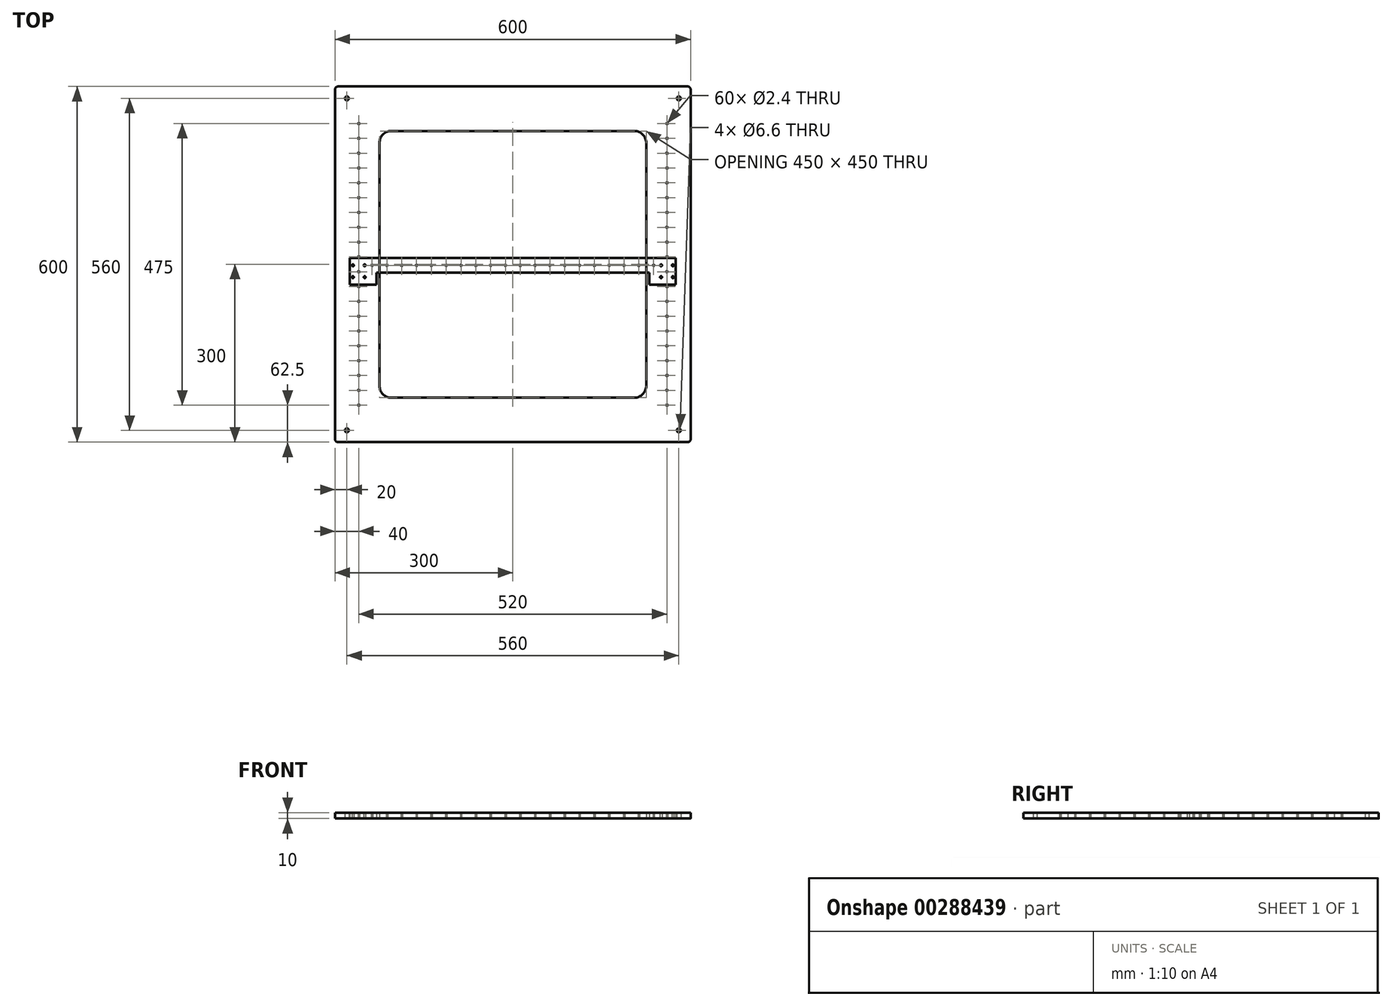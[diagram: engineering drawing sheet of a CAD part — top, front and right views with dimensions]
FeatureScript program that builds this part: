
annotation { "Feature Type Name" : "Feature", "Feature Type Description" : "" }
export const myFeature = defineFeature(function(context is Context, id is Id, definition is map)
    precondition{}
    {
        {
            var Q0;
            Q0=qCreatedBy(makeId("Top.planeOp"),FACE);
            var sketch = newSketch(context, id + "F0", { "sketchPlane" : qUnion([Q0])});
            skLineSegment(sketch, "E0.bottom", {"start": v(-295, 300) * mm, "end": v(295, 300) * mm});
            skLineSegment(sketch, "E0.top", {"start": v(-295, -300) * mm, "end": v(295, -300) * mm});
            skLineSegment(sketch, "E0.left", {"start": v(-300, 295) * mm, "end": v(-300, -295) * mm});
            skLineSegment(sketch, "E0.right", {"start": v(300, 295) * mm, "end": v(300, -295) * mm});
            skLineSegment(sketch, "E1", {"start": v(-260, 250) * mm, "end": v(-260, -250) * mm, "construction": true});
            skPoint(sketch, "E2", {"position": v(-260, -237.5) * mm});
            skPoint(sketch, "E3.0.1.0", {"position": v(-260, -212.5) * mm});
            skPoint(sketch, "E3.0.2.0", {"position": v(-260, -187.5) * mm});
            skPoint(sketch, "E3.0.3.0", {"position": v(-260, -162.5) * mm});
            skPoint(sketch, "E3.0.4.0", {"position": v(-260, -137.5) * mm});
            skPoint(sketch, "E3.0.5.0", {"position": v(-260, -112.5) * mm});
            skPoint(sketch, "E3.0.6.0", {"position": v(-260, -87.5) * mm});
            skPoint(sketch, "E3.0.7.0", {"position": v(-260, -62.5) * mm});
            skPoint(sketch, "E3.0.8.0", {"position": v(-260, -37.5) * mm});
            skPoint(sketch, "E3.0.9.0", {"position": v(-260, -12.5) * mm});
            skPoint(sketch, "E3.0.10.0", {"position": v(-260, 12.5) * mm});
            skPoint(sketch, "E3.0.11.0", {"position": v(-260, 37.5) * mm});
            skPoint(sketch, "E3.0.12.0", {"position": v(-260, 62.5) * mm});
            skPoint(sketch, "E3.0.13.0", {"position": v(-260, 87.5) * mm});
            skPoint(sketch, "E3.0.14.0", {"position": v(-260, 112.5) * mm});
            skPoint(sketch, "E3.0.15.0", {"position": v(-260, 137.5) * mm});
            skPoint(sketch, "E3.0.16.0", {"position": v(-260, 162.5) * mm});
            skPoint(sketch, "E3.0.17.0", {"position": v(-260, 187.5) * mm});
            skPoint(sketch, "E3.0.18.0", {"position": v(-260, 212.5) * mm});
            skPoint(sketch, "E3.0.19.0", {"position": v(-260, 237.5) * mm});
            skLineSegment(sketch, "E3.direction1", {"start": v(-260, -237.5) * mm, "end": v(-225.8, -237.5) * mm, "construction": true});
            skLineSegment(sketch, "E3.direction2", {"start": v(-260, -237.5) * mm, "end": v(-260, -212.5) * mm, "construction": true});
            skPoint(sketch, "E4.MirrorP", {"position": v(260, 237.5) * mm});
            skPoint(sketch, "E5.MirrorP", {"position": v(260, 212.5) * mm});
            skPoint(sketch, "E6.MirrorP", {"position": v(260, 187.5) * mm});
            skPoint(sketch, "E7.MirrorP", {"position": v(260, 162.5) * mm});
            skPoint(sketch, "E8.MirrorP", {"position": v(260, 137.5) * mm});
            skPoint(sketch, "E9.MirrorP", {"position": v(260, 112.5) * mm});
            skPoint(sketch, "E10.MirrorP", {"position": v(260, 87.5) * mm});
            skPoint(sketch, "E11.MirrorP", {"position": v(260, 62.5) * mm});
            skPoint(sketch, "E12.MirrorP", {"position": v(260, 37.5) * mm});
            skPoint(sketch, "E13.MirrorP", {"position": v(260, 12.5) * mm});
            skPoint(sketch, "E14.MirrorP", {"position": v(260, -12.5) * mm});
            skPoint(sketch, "E15.MirrorP", {"position": v(260, -37.5) * mm});
            skPoint(sketch, "E16.MirrorP", {"position": v(260, -62.5) * mm});
            skPoint(sketch, "E17.MirrorP", {"position": v(260, -87.5) * mm});
            skPoint(sketch, "E18.MirrorP", {"position": v(260, -112.5) * mm});
            skPoint(sketch, "E19.MirrorP", {"position": v(260, -137.5) * mm});
            skPoint(sketch, "E20.MirrorP", {"position": v(260, -162.5) * mm});
            skPoint(sketch, "E21.MirrorP", {"position": v(260, -187.5) * mm});
            skPoint(sketch, "E22.MirrorP", {"position": v(260, -212.5) * mm});
            skPoint(sketch, "E23.MirrorP", {"position": v(260, -237.5) * mm});
            skLineSegment(sketch, "E24.bottom", {"start": v(-295, -300) * mm, "end": v(-260, -300) * mm, "construction": true});
            skLineSegment(sketch, "E24.top", {"start": v(-300, -260) * mm, "end": v(-260, -260) * mm, "construction": true});
            skLineSegment(sketch, "E24.left", {"start": v(-300, -295) * mm, "end": v(-300, -260) * mm, "construction": true});
            skLineSegment(sketch, "E24.right", {"start": v(-260, -300) * mm, "end": v(-260, -260) * mm, "construction": true});
            skLineSegment(sketch, "E25.bottom", {"start": v(-300, 300) * mm, "end": v(-260, 300) * mm, "construction": true});
            skLineSegment(sketch, "E25.top", {"start": v(-300, 260) * mm, "end": v(-260, 260) * mm, "construction": true});
            skLineSegment(sketch, "E25.left", {"start": v(-300, 300) * mm, "end": v(-300, 260) * mm, "construction": true});
            skLineSegment(sketch, "E25.right", {"start": v(-260, 300) * mm, "end": v(-260, 260) * mm, "construction": true});
            skLineSegment(sketch, "E26.bottom", {"start": v(-205, -225) * mm, "end": v(205, -225) * mm});
            skLineSegment(sketch, "E26.top", {"start": v(-205, 225) * mm, "end": v(205, 225) * mm});
            skLineSegment(sketch, "E26.left", {"start": v(-225, -205) * mm, "end": v(-225, 205) * mm});
            skLineSegment(sketch, "E26.right", {"start": v(225, -205) * mm, "end": v(225, 205) * mm});
            skPoint(sketch, "E27.visualSharp", {"position": v(-300, -300) * mm});
            skArc(sketch, "E27.filletArc", {"start": v(-300, -295) * mm, "mid": v(-298.54, -298.54) * mm, "end": v(-295, -300) * mm, "construction": true});
            skArc(sketch, "E28.filletArc", {"start": v(-300, -295) * mm, "mid": v(-298.54, -298.54) * mm, "end": v(-295, -300) * mm});
            skPoint(sketch, "E29.visualSharp", {"position": v(300, -300) * mm});
            skArc(sketch, "E29.filletArc", {"start": v(295, -300) * mm, "mid": v(298.54, -298.54) * mm, "end": v(300, -295) * mm});
            skPoint(sketch, "E30.visualSharp", {"position": v(300, 300) * mm});
            skArc(sketch, "E30.filletArc", {"start": v(300, 295) * mm, "mid": v(298.54, 298.54) * mm, "end": v(295, 300) * mm});
            skPoint(sketch, "E31.visualSharp", {"position": v(-300, 300) * mm});
            skArc(sketch, "E31.filletArc", {"start": v(-295, 300) * mm, "mid": v(-298.54, 298.54) * mm, "end": v(-300, 295) * mm});
            skPoint(sketch, "E32.visualSharp", {"position": v(-225, 225) * mm});
            skArc(sketch, "E32.filletArc", {"start": v(-205, 225) * mm, "mid": v(-219.14, 219.14) * mm, "end": v(-225, 205) * mm});
            skPoint(sketch, "E33.visualSharp", {"position": v(225, 225) * mm});
            skArc(sketch, "E33.filletArc", {"start": v(225, 205) * mm, "mid": v(219.14, 219.14) * mm, "end": v(205, 225) * mm});
            skPoint(sketch, "E34.visualSharp", {"position": v(225, -225) * mm});
            skArc(sketch, "E34.filletArc", {"start": v(205, -225) * mm, "mid": v(219.14, -219.14) * mm, "end": v(225, -205) * mm});
            skPoint(sketch, "E35.visualSharp", {"position": v(-225, -225) * mm});
            skArc(sketch, "E35.filletArc", {"start": v(-225, -205) * mm, "mid": v(-219.14, -219.14) * mm, "end": v(-205, -225) * mm});
            skPoint(sketch, "E36", {"position": v(-280, 280) * mm});
            skPoint(sketch, "E37", {"position": v(-280, -280) * mm});
            skPoint(sketch, "E38", {"position": v(280, -280) * mm});
            skPoint(sketch, "E39", {"position": v(280, 280) * mm});
            skSolve(sketch);
        }
        {
            var Q0;
            Q0=makeQuery(id+"F0.imprint","IMPRINT",FACE,{"disambiguationData":[TD([[makeQuery(id+"F0.imprint","IMPRINT",EDGE,{"derivedFrom":sQuery(id+"F0.wireOp",EDGE,"E0.bottom")}),-1.0]])]});
            extrude(context, id + "F1", {"entities" : qUnion([Q0]), "depth" : 10 * mm});
        }
        {
            var Q0;
            Q0=sQuery(id+"F0.wireOp",VERTEX,"E3.0.19.0");
            var Q1;
            Q1=sQuery(id+"F0.wireOp",VERTEX,"E3.0.18.0");
            var Q2;
            Q2=sQuery(id+"F0.wireOp",VERTEX,"E3.0.17.0");
            var Q3;
            Q3=sQuery(id+"F0.wireOp",VERTEX,"E3.0.16.0");
            var Q4;
            Q4=sQuery(id+"F0.wireOp",VERTEX,"E3.0.15.0");
            var Q5;
            Q5=sQuery(id+"F0.wireOp",VERTEX,"E3.0.14.0");
            var Q6;
            Q6=sQuery(id+"F0.wireOp",VERTEX,"E3.0.13.0");
            var Q7;
            Q7=sQuery(id+"F0.wireOp",VERTEX,"E3.0.12.0");
            var Q8;
            Q8=sQuery(id+"F0.wireOp",VERTEX,"E3.0.11.0");
            var Q9;
            Q9=sQuery(id+"F0.wireOp",VERTEX,"E3.0.10.0");
            var Q10;
            Q10=sQuery(id+"F0.wireOp",VERTEX,"E3.0.9.0");
            var Q11;
            Q11=sQuery(id+"F0.wireOp",VERTEX,"E3.0.8.0");
            var Q12;
            Q12=sQuery(id+"F0.wireOp",VERTEX,"E3.0.7.0");
            var Q13;
            Q13=sQuery(id+"F0.wireOp",VERTEX,"E3.0.6.0");
            var Q14;
            Q14=sQuery(id+"F0.wireOp",VERTEX,"E3.0.5.0");
            var Q15;
            Q15=sQuery(id+"F0.wireOp",VERTEX,"E3.0.4.0");
            var Q16;
            Q16=sQuery(id+"F0.wireOp",VERTEX,"E3.0.3.0");
            var Q17;
            Q17=sQuery(id+"F0.wireOp",VERTEX,"E3.0.2.0");
            var Q18;
            Q18=sQuery(id+"F0.wireOp",VERTEX,"E3.0.1.0");
            var Q19;
            Q19=sQuery(id+"F0.wireOp",VERTEX,"E2");
            var Q20;
            Q20=sQuery(id+"F0.wireOp",VERTEX,"E6.MirrorP");
            var Q21;
            Q21=sQuery(id+"F0.wireOp",VERTEX,"E21.MirrorP");
            var Q22;
            Q22=sQuery(id+"F0.wireOp",VERTEX,"E11.MirrorP");
            var Q23;
            Q23=sQuery(id+"F0.wireOp",VERTEX,"E23.MirrorP");
            var Q24;
            Q24=sQuery(id+"F0.wireOp",VERTEX,"E13.MirrorP");
            var Q25;
            Q25=sQuery(id+"F0.wireOp",VERTEX,"E15.MirrorP");
            var Q26;
            Q26=sQuery(id+"F0.wireOp",VERTEX,"E8.MirrorP");
            var Q27;
            Q27=sQuery(id+"F0.wireOp",VERTEX,"E19.MirrorP");
            var Q28;
            Q28=sQuery(id+"F0.wireOp",VERTEX,"E4.MirrorP");
            var Q29;
            Q29=sQuery(id+"F0.wireOp",VERTEX,"E9.MirrorP");
            var Q30;
            Q30=sQuery(id+"F0.wireOp",VERTEX,"E16.MirrorP");
            var Q31;
            Q31=sQuery(id+"F0.wireOp",VERTEX,"E14.MirrorP");
            var Q32;
            Q32=sQuery(id+"F0.wireOp",VERTEX,"E7.MirrorP");
            var Q33;
            Q33=sQuery(id+"F0.wireOp",VERTEX,"E22.MirrorP");
            var Q34;
            Q34=sQuery(id+"F0.wireOp",VERTEX,"E12.MirrorP");
            var Q35;
            Q35=sQuery(id+"F0.wireOp",VERTEX,"E10.MirrorP");
            var Q36;
            Q36=sQuery(id+"F0.wireOp",VERTEX,"E20.MirrorP");
            var Q37;
            Q37=sQuery(id+"F0.wireOp",VERTEX,"E5.MirrorP");
            var Q38;
            Q38=sQuery(id+"F0.wireOp",VERTEX,"E18.MirrorP");
            var Q39;
            Q39=sQuery(id+"F0.wireOp",VERTEX,"E17.MirrorP");
            var Q40;
            Q40=makeQuery(id+"F1.opExtrude","SWEPT_BODY",BODY,{"disambiguationData":[OSD([sQuery(id+"F0.wireOp",EDGE,"E0.bottom"),sQuery(id+"F0.wireOp",EDGE,"E0.top"),sQuery(id+"F0.wireOp",EDGE,"E0.left"),sQuery(id+"F0.wireOp",EDGE,"E0.right"),sQuery(id+"F0.wireOp",EDGE,"E26.bottom"),sQuery(id+"F0.wireOp",EDGE,"E26.top"),sQuery(id+"F0.wireOp",EDGE,"E26.left"),sQuery(id+"F0.wireOp",EDGE,"E26.right")])]});
            hole(context, id + "F2", {"style" : HoleStyle.SIMPLE, "endStyle" : HoleEndStyle.BLIND, "oppositeDirection" : true, "standardTappedOrClearance" : lookupTablePath({ "standard" : "ISO", "engagement" : "75%", "pitch" : "0.6 mm", "size" : "M3", "type" : "Tapped" }), "standardBlindInLast" : lookupTablePath({ "standard" : "ISO", "engagement" : "75%", "pitch" : "0.6 mm", "size" : "M3", "type" : "Tapped" }), "holeDiameter" : 2.4 * mm, "showTappedDepth" : true, "holeDepth" : 20 * mm, "tappedDepth" : 20 * mm, "tapClearance" : 0, "locations" : qUnion([Q0, Q1, Q2, Q3, Q4, Q5, Q6, Q7, Q8, Q9, Q10, Q11, Q12, Q13, Q14, Q15, Q16, Q17, Q18, Q19, Q20, Q21, Q22, Q23, Q24, Q25, Q26, Q27, Q28, Q29, Q30, Q31, Q32, Q33, Q34, Q35, Q36, Q37, Q38, Q39]), "scope" : qUnion([Q40])});
        }
        {
            var Q0;
            Q0=qCreatedBy(makeId("Top.planeOp"),FACE);
            var sketch = newSketch(context, id + "F3", { "sketchPlane" : qUnion([Q0])});
            skLineSegment(sketch, "E40.bottom", {"start": v(-275, -14.18) * mm, "end": v(275, -14.18) * mm});
            skLineSegment(sketch, "E40.top", {"start": v(-275, 10.82) * mm, "end": v(275, 10.82) * mm});
            skLineSegment(sketch, "E40.left", {"start": v(-275, -14.18) * mm, "end": v(-275, 10.82) * mm});
            skLineSegment(sketch, "E40.right", {"start": v(275, -14.18) * mm, "end": v(275, 10.82) * mm});
            skLineSegment(sketch, "E41.bottom", {"start": v(-275, 10.82) * mm, "end": v(-230, 10.82) * mm});
            skLineSegment(sketch, "E41.top", {"start": v(-275, -34.18) * mm, "end": v(-230, -34.18) * mm});
            skLineSegment(sketch, "E41.left", {"start": v(-275, 10.82) * mm, "end": v(-275, -34.18) * mm});
            skLineSegment(sketch, "E41.right", {"start": v(-230, 10.82) * mm, "end": v(-230, -34.18) * mm});
            skLineSegment(sketch, "E42.bottom", {"start": v(275, 10.82) * mm, "end": v(230, 10.82) * mm});
            skLineSegment(sketch, "E42.top", {"start": v(275, -34.18) * mm, "end": v(230, -34.18) * mm});
            skLineSegment(sketch, "E42.left", {"start": v(275, 10.82) * mm, "end": v(275, -34.18) * mm});
            skLineSegment(sketch, "E42.right", {"start": v(230, 10.82) * mm, "end": v(230, -34.18) * mm});
            skSolve(sketch);
        }
        {
            var Q0;
            {var subQ5=sQuery(id+"F3.wireOp",EDGE,"E40.top");Q0=makeQuery(id+"F3.imprint","IMPRINT",FACE,{"disambiguationData":[TD([[makeQuery(id+"F3.imprint","IMPRINT",EDGE,{"derivedFrom":subQ5}),-1.0]])]});}
            var Q1;
            {var subQ5=sQuery(id+"F3.wireOp",EDGE,"E42.bottom");Q1=makeQuery(id+"F3.imprint","IMPRINT",FACE,{"disambiguationData":[TD([[makeQuery(id+"F3.imprint","IMPRINT",EDGE,{"derivedFrom":subQ5}),1.0]])]});}
            var Q2;
            {var subQ5=sQuery(id+"F3.wireOp",EDGE,"E42.top");Q2=makeQuery(id+"F3.imprint","IMPRINT",FACE,{"disambiguationData":[TD([[makeQuery(id+"F3.imprint","IMPRINT",EDGE,{"derivedFrom":subQ5}),-1.0]])]});}
            var Q3;
            {var subQ5=sQuery(id+"F3.wireOp",EDGE,"E41.bottom");Q3=makeQuery(id+"F3.imprint","IMPRINT",FACE,{"disambiguationData":[TD([[makeQuery(id+"F3.imprint","IMPRINT",EDGE,{"derivedFrom":subQ5}),-1.0]])]});}
            var Q4;
            {var subQ5=sQuery(id+"F3.wireOp",EDGE,"E41.top");Q4=makeQuery(id+"F3.imprint","IMPRINT",FACE,{"disambiguationData":[TD([[makeQuery(id+"F3.imprint","IMPRINT",EDGE,{"derivedFrom":subQ5}),1.0]])]});}
            extrude(context, id + "F4", {"entities" : qUnion([Q0, Q1, Q2, Q3, Q4]), "depth" : 10 * mm});
        }
        {
            var Q0;
            Q0=makeQuery(id+"F4.opExtrude","CAP_FACE",FACE,{"disambiguationData":[OSD([sQuery(id+"F3.wireOp",EDGE,"E40.bottom"),sQuery(id+"F3.wireOp",EDGE,"E40.top"),sQuery(id+"F3.wireOp",EDGE,"E41.bottom"),sQuery(id+"F3.wireOp",EDGE,"E41.top"),sQuery(id+"F3.wireOp",EDGE,"E41.left"),sQuery(id+"F3.wireOp",EDGE,"E41.right"),sQuery(id+"F3.wireOp",EDGE,"E42.bottom"),sQuery(id+"F3.wireOp",EDGE,"E42.top"),sQuery(id+"F3.wireOp",EDGE,"E42.left"),sQuery(id+"F3.wireOp",EDGE,"E42.right")])],"isStart":true});
            var sketch = newSketch(context, id + "F5", { "sketchPlane" : qUnion([Q0])});
            skLineSegment(sketch, "E43", {"start": v(-250, 1.68) * mm, "end": v(250, 1.68) * mm, "construction": true});
            skPoint(sketch, "E44", {"position": v(-237.5, 1.68) * mm});
            skPoint(sketch, "E45.1.0.0", {"position": v(-212.5, 1.68) * mm});
            skPoint(sketch, "E45.2.0.0", {"position": v(-187.5, 1.68) * mm});
            skPoint(sketch, "E45.3.0.0", {"position": v(-162.5, 1.68) * mm});
            skPoint(sketch, "E45.4.0.0", {"position": v(-137.5, 1.68) * mm});
            skPoint(sketch, "E45.5.0.0", {"position": v(-112.5, 1.68) * mm});
            skPoint(sketch, "E45.6.0.0", {"position": v(-87.5, 1.68) * mm});
            skPoint(sketch, "E45.7.0.0", {"position": v(-62.5, 1.68) * mm});
            skPoint(sketch, "E45.8.0.0", {"position": v(-37.5, 1.68) * mm});
            skPoint(sketch, "E45.9.0.0", {"position": v(-12.5, 1.68) * mm});
            skPoint(sketch, "E45.10.0.0", {"position": v(12.5, 1.68) * mm});
            skPoint(sketch, "E45.11.0.0", {"position": v(37.5, 1.68) * mm});
            skPoint(sketch, "E45.12.0.0", {"position": v(62.5, 1.68) * mm});
            skPoint(sketch, "E45.13.0.0", {"position": v(87.5, 1.68) * mm});
            skPoint(sketch, "E45.14.0.0", {"position": v(112.5, 1.68) * mm});
            skPoint(sketch, "E45.15.0.0", {"position": v(137.5, 1.68) * mm});
            skPoint(sketch, "E45.16.0.0", {"position": v(162.5, 1.68) * mm});
            skPoint(sketch, "E45.17.0.0", {"position": v(187.5, 1.68) * mm});
            skPoint(sketch, "E45.18.0.0", {"position": v(212.5, 1.68) * mm});
            skPoint(sketch, "E45.19.0.0", {"position": v(237.5, 1.68) * mm});
            skLineSegment(sketch, "E45.direction1", {"start": v(-237.5, 1.68) * mm, "end": v(-212.5, 1.68) * mm, "construction": true});
            skSolve(sketch);
        }
        {
            var Q0;
            Q0=sQuery(id+"F5.wireOp",VERTEX,"E45.9.0.0");
            var Q1;
            Q1=sQuery(id+"F5.wireOp",VERTEX,"E45.10.0.0");
            var Q2;
            Q2=sQuery(id+"F5.wireOp",VERTEX,"E45.11.0.0");
            var Q3;
            Q3=sQuery(id+"F5.wireOp",VERTEX,"E45.19.0.0");
            var Q4;
            Q4=sQuery(id+"F5.wireOp",VERTEX,"E45.4.0.0");
            var Q5;
            Q5=sQuery(id+"F5.wireOp",VERTEX,"E45.3.0.0");
            var Q6;
            Q6=sQuery(id+"F5.wireOp",VERTEX,"E45.6.0.0");
            var Q7;
            Q7=sQuery(id+"F5.wireOp",VERTEX,"E45.5.0.0");
            var Q8;
            Q8=sQuery(id+"F5.wireOp",VERTEX,"E45.8.0.0");
            var Q9;
            Q9=sQuery(id+"F5.wireOp",VERTEX,"E45.7.0.0");
            var Q10;
            Q10=sQuery(id+"F5.wireOp",VERTEX,"E45.13.0.0");
            var Q11;
            Q11=sQuery(id+"F5.wireOp",VERTEX,"E45.12.0.0");
            var Q12;
            Q12=sQuery(id+"F5.wireOp",VERTEX,"E45.15.0.0");
            var Q13;
            Q13=sQuery(id+"F5.wireOp",VERTEX,"E45.14.0.0");
            var Q14;
            Q14=sQuery(id+"F5.wireOp",VERTEX,"E45.17.0.0");
            var Q15;
            Q15=sQuery(id+"F5.wireOp",VERTEX,"E44");
            var Q16;
            Q16=sQuery(id+"F5.wireOp",VERTEX,"E45.16.0.0");
            var Q17;
            Q17=sQuery(id+"F5.wireOp",VERTEX,"E45.2.0.0");
            var Q18;
            Q18=sQuery(id+"F5.wireOp",VERTEX,"E45.18.0.0");
            var Q19;
            Q19=sQuery(id+"F5.wireOp",VERTEX,"E45.1.0.0");
            var Q20;
            Q20=makeQuery(id+"F4.opExtrude","SWEPT_BODY",BODY,{"disambiguationData":[OSD([sQuery(id+"F3.wireOp",EDGE,"E40.bottom"),sQuery(id+"F3.wireOp",EDGE,"E40.top"),sQuery(id+"F3.wireOp",EDGE,"E41.bottom"),sQuery(id+"F3.wireOp",EDGE,"E41.top"),sQuery(id+"F3.wireOp",EDGE,"E41.left"),sQuery(id+"F3.wireOp",EDGE,"E41.right"),sQuery(id+"F3.wireOp",EDGE,"E42.bottom"),sQuery(id+"F3.wireOp",EDGE,"E42.top"),sQuery(id+"F3.wireOp",EDGE,"E42.left"),sQuery(id+"F3.wireOp",EDGE,"E42.right")])]});
            hole(context, id + "F6", {"style" : HoleStyle.SIMPLE, "endStyle" : HoleEndStyle.BLIND, "standardTappedOrClearance" : lookupTablePath({ "standard" : "ISO", "engagement" : "75%", "pitch" : "0.6 mm", "size" : "M3", "type" : "Tapped" }), "standardBlindInLast" : lookupTablePath({ "standard" : "ISO", "engagement" : "75%", "pitch" : "0.6 mm", "size" : "M3", "type" : "Tapped" }), "holeDiameter" : 2.4 * mm, "showTappedDepth" : true, "holeDepth" : 20 * mm, "tappedDepth" : 20 * mm, "tapClearance" : 0, "locations" : qUnion([Q0, Q1, Q2, Q3, Q4, Q5, Q6, Q7, Q8, Q9, Q10, Q11, Q12, Q13, Q14, Q15, Q16, Q17, Q18, Q19]), "scope" : qUnion([Q20])});
        }
        {
            var Q0;
            Q0=makeQuery(id+"F4.opExtrude","CAP_FACE",FACE,{"disambiguationData":[OSD([sQuery(id+"F3.wireOp",EDGE,"E40.bottom"),sQuery(id+"F3.wireOp",EDGE,"E40.top"),sQuery(id+"F3.wireOp",EDGE,"E41.bottom"),sQuery(id+"F3.wireOp",EDGE,"E41.top"),sQuery(id+"F3.wireOp",EDGE,"E41.left"),sQuery(id+"F3.wireOp",EDGE,"E41.right"),sQuery(id+"F3.wireOp",EDGE,"E42.bottom"),sQuery(id+"F3.wireOp",EDGE,"E42.top"),sQuery(id+"F3.wireOp",EDGE,"E42.left"),sQuery(id+"F3.wireOp",EDGE,"E42.right")])],"isStart":true});
            var sketch = newSketch(context, id + "F7", { "sketchPlane" : qUnion([Q0])});
            skLineSegment(sketch, "E46", {"start": v(-260, 61.36) * mm, "end": v(260, 61.36) * mm, "construction": true});
            skLineSegment(sketch, "E47", {"start": v(-260, 61.36) * mm, "end": v(-260, -74.35) * mm, "construction": true});
            skLineSegment(sketch, "E48", {"start": v(-260, -74.35) * mm, "end": v(260, -74.35) * mm, "construction": true});
            skLineSegment(sketch, "E49", {"start": v(260, -74.35) * mm, "end": v(260, 61.36) * mm, "construction": true});
            skPoint(sketch, "E50", {"position": v(-270, 21.68) * mm});
            skPoint(sketch, "E51", {"position": v(-270, 1.68) * mm});
            skPoint(sketch, "E52", {"position": v(-250, 1.68) * mm});
            skPoint(sketch, "E53", {"position": v(-250, 21.68) * mm});
            skLineSegment(sketch, "E54", {"start": v(-275, 11.68) * mm, "end": v(-247.45, 11.68) * mm, "construction": true});
            skPoint(sketch, "E55.MirrorP", {"position": v(250, 21.68) * mm});
            skPoint(sketch, "E56.MirrorP", {"position": v(250, 1.68) * mm});
            skPoint(sketch, "E57.MirrorP", {"position": v(270, 1.68) * mm});
            skPoint(sketch, "E58.MirrorP", {"position": v(270, 21.68) * mm});
            skSolve(sketch);
        }
        {
            var Q0;
            Q0=sQuery(id+"F7.wireOp",VERTEX,"E50");
            var Q1;
            Q1=sQuery(id+"F7.wireOp",VERTEX,"E51");
            var Q2;
            Q2=sQuery(id+"F7.wireOp",VERTEX,"E53");
            var Q3;
            Q3=sQuery(id+"F7.wireOp",VERTEX,"E55.MirrorP");
            var Q4;
            Q4=sQuery(id+"F7.wireOp",VERTEX,"E56.MirrorP");
            var Q5;
            Q5=sQuery(id+"F7.wireOp",VERTEX,"E57.MirrorP");
            var Q6;
            Q6=sQuery(id+"F7.wireOp",VERTEX,"E58.MirrorP");
            var Q7;
            Q7=sQuery(id+"F7.wireOp",VERTEX,"E52");
            var Q8;
            Q8=makeQuery(id+"F4.opExtrude","SWEPT_BODY",BODY,{"disambiguationData":[OSD([sQuery(id+"F3.wireOp",EDGE,"E40.bottom"),sQuery(id+"F3.wireOp",EDGE,"E40.top"),sQuery(id+"F3.wireOp",EDGE,"E41.bottom"),sQuery(id+"F3.wireOp",EDGE,"E41.top"),sQuery(id+"F3.wireOp",EDGE,"E41.left"),sQuery(id+"F3.wireOp",EDGE,"E41.right"),sQuery(id+"F3.wireOp",EDGE,"E42.bottom"),sQuery(id+"F3.wireOp",EDGE,"E42.top"),sQuery(id+"F3.wireOp",EDGE,"E42.left"),sQuery(id+"F3.wireOp",EDGE,"E42.right")])]});
            hole(context, id + "F8", {"style" : HoleStyle.SIMPLE, "endStyle" : HoleEndStyle.BLIND, "holeDiameter" : 3.3 * mm, "holeDepth" : 20 * mm, "tappedDepth" : 20 * mm, "tapClearance" : 0, "locations" : qUnion([Q0, Q1, Q2, Q3, Q4, Q5, Q6, Q7]), "scope" : qUnion([Q8])});
        }
        {
            var Q0;
            Q0=sQuery(id+"F0.wireOp",VERTEX,"E36");
            var Q1;
            Q1=sQuery(id+"F0.wireOp",VERTEX,"E37");
            var Q2;
            Q2=sQuery(id+"F0.wireOp",VERTEX,"E38");
            var Q3;
            Q3=sQuery(id+"F0.wireOp",VERTEX,"E39");
            var Q4;
            Q4=makeQuery(id+"F1.opExtrude","SWEPT_BODY",BODY,{"disambiguationData":[OSD([sQuery(id+"F0.wireOp",EDGE,"E0.bottom"),sQuery(id+"F0.wireOp",EDGE,"E0.top"),sQuery(id+"F0.wireOp",EDGE,"E0.left"),sQuery(id+"F0.wireOp",EDGE,"E0.right"),sQuery(id+"F0.wireOp",EDGE,"E26.bottom"),sQuery(id+"F0.wireOp",EDGE,"E26.top"),sQuery(id+"F0.wireOp",EDGE,"E26.left"),sQuery(id+"F0.wireOp",EDGE,"E26.right"),sQuery(id+"F0.wireOp",EDGE,"E28.filletArc"),sQuery(id+"F0.wireOp",EDGE,"E29.filletArc"),sQuery(id+"F0.wireOp",EDGE,"E30.filletArc"),sQuery(id+"F0.wireOp",EDGE,"E31.filletArc"),sQuery(id+"F0.wireOp",EDGE,"E32.filletArc"),sQuery(id+"F0.wireOp",EDGE,"E33.filletArc"),sQuery(id+"F0.wireOp",EDGE,"E34.filletArc"),sQuery(id+"F0.wireOp",EDGE,"E35.filletArc")])]});
            hole(context, id + "F9", {"style" : HoleStyle.SIMPLE, "endStyle" : HoleEndStyle.BLIND, "oppositeDirection" : true, "standardTappedOrClearance" : lookupTablePath({ "standard" : "ISO", "fit" : "Normal", "size" : "M6", "type" : "Clearance" }), "standardBlindInLast" : lookupTablePath({ "fit" : "Standard", "standard" : "ISO", "size" : "M6", "type" : "Clearance" }), "holeDiameter" : 6.6 * mm, "holeDepth" : 20 * mm, "tappedDepth" : 20 * mm, "tapClearance" : 0, "locations" : qUnion([Q0, Q1, Q2, Q3]), "scope" : qUnion([Q4])});
        }
    });
